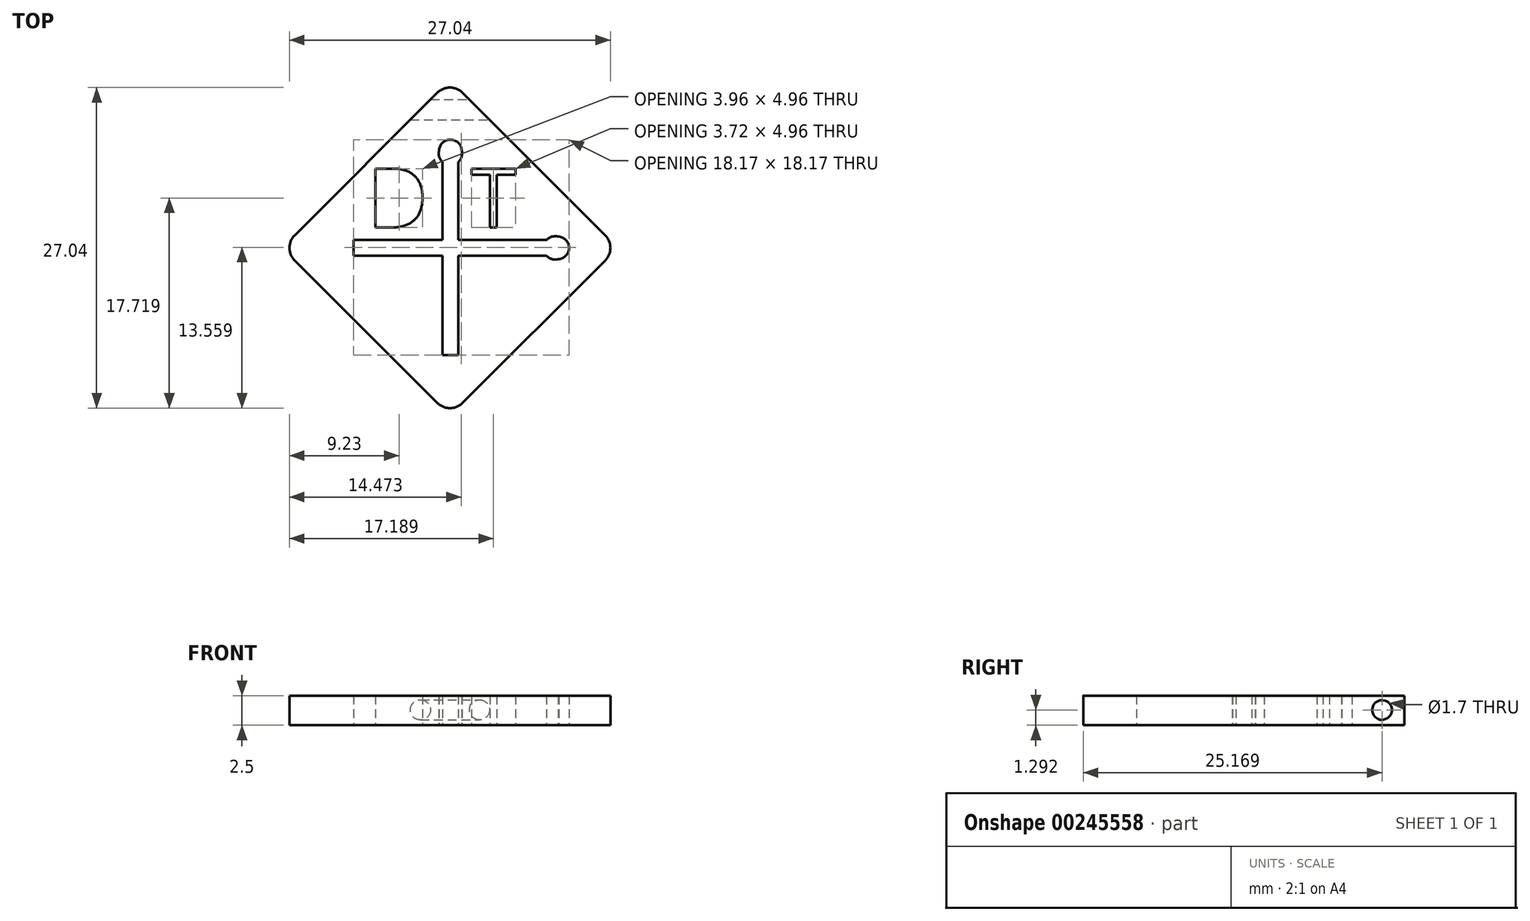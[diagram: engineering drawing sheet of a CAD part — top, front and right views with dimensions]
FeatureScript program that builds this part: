
annotation { "Feature Type Name" : "Feature", "Feature Type Description" : "" }
export const myFeature = defineFeature(function(context is Context, id is Id, definition is map)
    precondition{}
    {
        {
            var Q0;
            Q0=qCreatedBy(makeId("Top.planeOp"),FACE);
            var sketch = newSketch(context, id + "F0", { "sketchPlane" : qUnion([Q0])});
            skLineSegment(sketch, "E0", {"start": v(1.06, -1.06) * mm, "end": v(13.08, -13.08) * mm});
            skLineSegment(sketch, "E1", {"start": v(13.08, -15.2) * mm, "end": v(1.06, -27.22) * mm});
            skLineSegment(sketch, "E2", {"start": v(-1.06, -27.22) * mm, "end": v(-13.08, -15.2) * mm});
            skLineSegment(sketch, "E3", {"start": v(-13.08, -13.08) * mm, "end": v(-1.06, -1.06) * mm});
            skPoint(sketch, "E4.visualSharp", {"position": v(0, 0) * mm});
            skArc(sketch, "E4.filletArc", {"start": v(1.06, -1.06) * mm, "mid": v(0, -0.62) * mm, "end": v(-1.06, -1.06) * mm});
            skPoint(sketch, "E5.visualSharp", {"position": v(-14.14, -14.14) * mm});
            skArc(sketch, "E5.filletArc", {"start": v(-13.08, -13.08) * mm, "mid": v(-13.52, -14.14) * mm, "end": v(-13.08, -15.2) * mm});
            skPoint(sketch, "E6.visualSharp", {"position": v(14.14, -14.14) * mm});
            skArc(sketch, "E6.filletArc", {"start": v(13.08, -15.2) * mm, "mid": v(13.52, -14.14) * mm, "end": v(13.08, -13.08) * mm});
            skPoint(sketch, "E7.visualSharp", {"position": v(0, -28.28) * mm});
            skArc(sketch, "E7.filletArc", {"start": v(-1.06, -27.22) * mm, "mid": v(0, -27.66) * mm, "end": v(1.06, -27.22) * mm});
            skLineSegment(sketch, "E8", {"start": v(0, 0) * mm, "end": v(0, -31.86) * mm, "construction": true});
            skLineSegment(sketch, "E9", {"start": v(-14.14, -14.14) * mm, "end": v(14.14, -14.14) * mm, "construction": true});
            skLineSegment(sketch, "E10", {"start": v(-8.13, -13.48) * mm, "end": v(-8.13, -14.8) * mm});
            skLineSegment(sketch, "E11", {"start": v(-8.13, -14.8) * mm, "end": v(8.13, -14.8) * mm});
            skLineSegment(sketch, "E12", {"start": v(8.13, -13.48) * mm, "end": v(-8.13, -13.48) * mm});
            skLineSegment(sketch, "E13", {"start": v(-8.13, -13.48) * mm, "end": v(0, -13.48) * mm, "construction": true});
            skLineSegment(sketch, "E14", {"start": v(0, -13.48) * mm, "end": v(8.13, -13.48) * mm, "construction": true});
            skArc(sketch, "E15", {"start": v(9.18, -15.1) * mm, "mid": v(10.04, -14.12) * mm, "end": v(9.13, -13.2) * mm});
            skArc(sketch, "E16", {"start": v(9.13, -13.2) * mm, "mid": v(8.6, -13.2) * mm, "end": v(8.13, -13.48) * mm});
            skArc(sketch, "E17", {"start": v(8.13, -14.8) * mm, "mid": v(8.61, -15.1) * mm, "end": v(9.18, -15.1) * mm});
            skLineSegment(sketch, "E18", {"start": v(-0.62, -23.19) * mm, "end": v(0.7, -23.19) * mm});
            skLineSegment(sketch, "E19", {"start": v(0.7, -23.19) * mm, "end": v(0.7, -6.92) * mm});
            skLineSegment(sketch, "E20", {"start": v(-0.62, -6.92) * mm, "end": v(-0.62, -23.19) * mm});
            skLineSegment(sketch, "E21", {"start": v(-0.62, -23.19) * mm, "end": v(-0.62, -15.05) * mm, "construction": true});
            skLineSegment(sketch, "E22", {"start": v(-0.62, -15.05) * mm, "end": v(-0.62, -6.92) * mm, "construction": true});
            skArc(sketch, "E23", {"start": v(0.99, -5.88) * mm, "mid": v(0.02, -5.01) * mm, "end": v(-0.91, -5.92) * mm});
            skArc(sketch, "E24", {"start": v(-0.91, -5.92) * mm, "mid": v(-0.9, -6.46) * mm, "end": v(-0.62, -6.92) * mm});
            skArc(sketch, "E25", {"start": v(0.7, -6.92) * mm, "mid": v(1, -6.44) * mm, "end": v(0.99, -5.88) * mm});
            skText(sketch, "E26", { "text": "D\n", "fontName": "OpenSans-Regular.ttf"});
            skText(sketch, "E27", { "text": "T", "fontName": "OpenSans-Regular.ttf"});
            const initialGuessF0  = {"E26": [-0.00695, -0.01242, 1, 0, 0.005], "E27": [0.00175, -0.01242, 1, 0, 0.005]};
            skSetInitialGuess(sketch, initialGuessF0);
            skSolve(sketch);
        }
        {
            var Q0;
            Q0=makeQuery(id+"F0.imprint","IMPRINT",FACE,{"disambiguationData":[TD([[makeQuery(id+"F0.imprint","IMPRINT",EDGE,{"derivedFrom":sQuery(id+"F0.wireOp",EDGE,"E0")}),-1.0]])]});
            extrude(context, id + "F1", {"entities" : qUnion([Q0]), "depth" : 2.5 * mm});
        }
        {
            var Q0;
            Q0=qCreatedBy(makeId("Right.planeOp"),FACE);
            var sketch = newSketch(context, id + "F2", { "sketchPlane" : qUnion([Q0])});
            skCircle(sketch, "E28", {"center": v(-2.5, 1.3) * mm, "radius": 0.85 * mm});
            skSolve(sketch);
        }
        {
            var Q0;
            Q0=qSketchRegion(id+"F2",true);
            extrude(context, id + "F3", {"entities" : qUnion([Q0]), "operationType" : NewBodyOperationType.REMOVE, "endBound" : BoundingType.SYMMETRIC, "oppositeDirection" : true, "depth" : 25 * mm});
        }
    });
